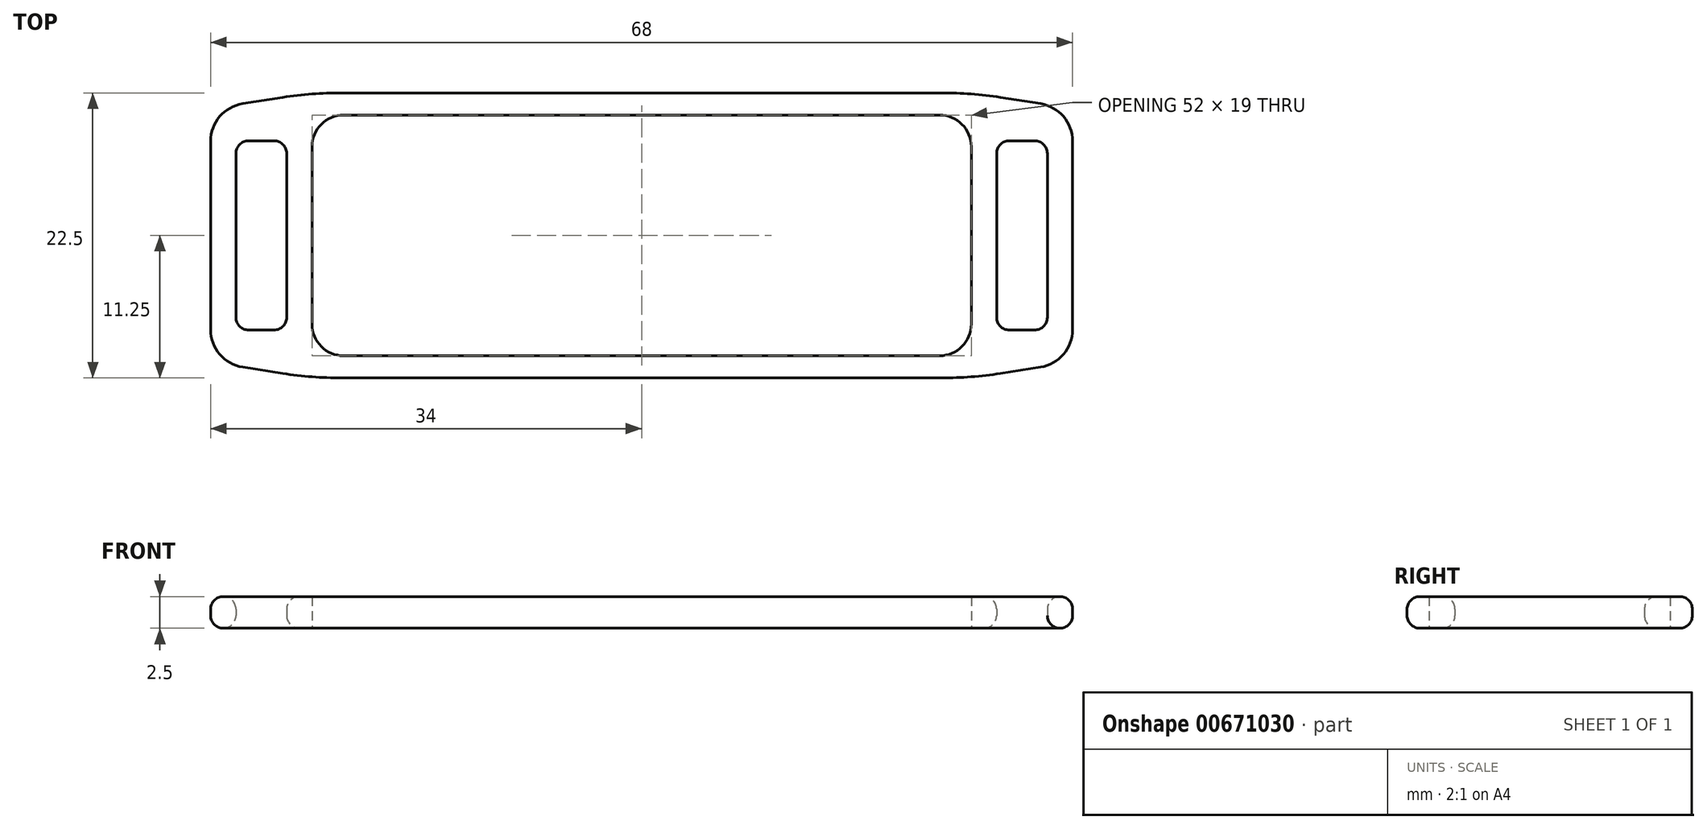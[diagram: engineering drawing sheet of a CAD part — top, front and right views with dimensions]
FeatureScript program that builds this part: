
annotation { "Feature Type Name" : "Feature", "Feature Type Description" : "" }
export const myFeature = defineFeature(function(context is Context, id is Id, definition is map)
    precondition{}
    {
        {
            var Q0;
            Q0=qCreatedBy(makeId("Top.planeOp"),FACE);
            var sketch = newSketch(context, id + "F0", { "sketchPlane" : qUnion([Q0])});
            skLineSegment(sketch, "E0.bottom", {"start": v(23.5, 9.5) * mm, "end": v(-23.5, 9.5) * mm});
            skLineSegment(sketch, "E0.top", {"start": v(23.5, -9.5) * mm, "end": v(-23.5, -9.5) * mm});
            skLineSegment(sketch, "E0.left", {"start": v(26, 7) * mm, "end": v(26, -7) * mm});
            skLineSegment(sketch, "E0.right", {"start": v(-26, 7) * mm, "end": v(-26, -7) * mm});
            skPoint(sketch, "E0.middle", {"position": v(0, 0) * mm});
            skPoint(sketch, "E1.visualSharp", {"position": v(-26, 9.5) * mm});
            skArc(sketch, "E1.filletArc", {"start": v(-23.5, 9.5) * mm, "mid": v(-25.27, 8.77) * mm, "end": v(-26, 7) * mm});
            skPoint(sketch, "E2.visualSharp", {"position": v(26, 9.5) * mm});
            skArc(sketch, "E2.filletArc", {"start": v(26, 7) * mm, "mid": v(25.27, 8.77) * mm, "end": v(23.5, 9.5) * mm});
            skPoint(sketch, "E3.visualSharp", {"position": v(26, -9.5) * mm});
            skArc(sketch, "E3.filletArc", {"start": v(23.5, -9.5) * mm, "mid": v(25.27, -8.77) * mm, "end": v(26, -7) * mm});
            skPoint(sketch, "E4.visualSharp", {"position": v(-26, -9.5) * mm});
            skArc(sketch, "E4.filletArc", {"start": v(-26, -7) * mm, "mid": v(-25.27, -8.77) * mm, "end": v(-23.5, -9.5) * mm});
            skLineSegment(sketch, "E5.bottom", {"start": v(34, -11.25) * mm, "end": v(-34, -11.25) * mm});
            skLineSegment(sketch, "E5.top", {"start": v(34, 11.25) * mm, "end": v(-34, 11.25) * mm});
            skLineSegment(sketch, "E5.left", {"start": v(34, -11.25) * mm, "end": v(34, 11.25) * mm});
            skLineSegment(sketch, "E5.right", {"start": v(-34, -11.25) * mm, "end": v(-34, 11.25) * mm});
            skLineSegment(sketch, "E6", {"start": v(26, 11.25) * mm, "end": v(34, 10) * mm});
            skLineSegment(sketch, "E7.MirrorCS", {"start": v(26, -11.25) * mm, "end": v(34, -10) * mm});
            skLineSegment(sketch, "E8.MirrorCS", {"start": v(-26, 11.25) * mm, "end": v(-34, 10) * mm});
            skLineSegment(sketch, "E9.MirrorCS", {"start": v(-26, -11.25) * mm, "end": v(-34, -10) * mm});
            skLineSegment(sketch, "E10.bottom", {"start": v(31, -7.47) * mm, "end": v(29, -7.47) * mm});
            skLineSegment(sketch, "E10.top", {"start": v(31, 7.47) * mm, "end": v(29, 7.47) * mm});
            skLineSegment(sketch, "E10.left", {"start": v(32, -6.47) * mm, "end": v(32, 6.47) * mm});
            skLineSegment(sketch, "E10.right", {"start": v(28, -6.47) * mm, "end": v(28, 6.47) * mm});
            skPoint(sketch, "E10.middle", {"position": v(30, 0) * mm});
            skPoint(sketch, "E11.visualSharp", {"position": v(32, 7.47) * mm});
            skArc(sketch, "E11.filletArc", {"start": v(32, 6.47) * mm, "mid": v(31.7, 7.18) * mm, "end": v(31, 7.47) * mm});
            skPoint(sketch, "E12.visualSharp", {"position": v(32, -7.47) * mm});
            skArc(sketch, "E12.filletArc", {"start": v(31, -7.47) * mm, "mid": v(31.7, -7.18) * mm, "end": v(32, -6.47) * mm});
            skPoint(sketch, "E13.visualSharp", {"position": v(28, -7.47) * mm});
            skArc(sketch, "E13.filletArc", {"start": v(28, -6.47) * mm, "mid": v(28.3, -7.18) * mm, "end": v(29, -7.47) * mm});
            skPoint(sketch, "E14.visualSharp", {"position": v(28, 7.47) * mm});
            skArc(sketch, "E14.filletArc", {"start": v(29, 7.47) * mm, "mid": v(28.3, 7.18) * mm, "end": v(28, 6.47) * mm});
            skLineSegment(sketch, "E15", {"start": v(31, -6.47) * mm, "end": v(31, -12.4) * mm, "construction": true});
            skPoint(sketch, "E16", {"position": v(31, -10.47) * mm});
            skArc(sketch, "E17.MirrorCS", {"start": v(-32, 6.47) * mm, "mid": v(-31.7, 7.18) * mm, "end": v(-31, 7.47) * mm});
            skArc(sketch, "E18.MirrorCS", {"start": v(-28, -6.47) * mm, "mid": v(-28.3, -7.18) * mm, "end": v(-29, -7.47) * mm});
            skArc(sketch, "E19.MirrorCS", {"start": v(-31, -7.47) * mm, "mid": v(-31.7, -7.18) * mm, "end": v(-32, -6.47) * mm});
            skArc(sketch, "E20.MirrorCS", {"start": v(-29, 7.47) * mm, "mid": v(-28.3, 7.18) * mm, "end": v(-28, 6.47) * mm});
            skPoint(sketch, "E21.MirrorP", {"position": v(-32, 7.47) * mm});
            skPoint(sketch, "E22.MirrorP", {"position": v(-32, -7.47) * mm});
            skLineSegment(sketch, "E23.MirrorCS", {"start": v(-32, -6.47) * mm, "end": v(-32, 6.47) * mm});
            skLineSegment(sketch, "E24.MirrorCS", {"start": v(-31, -7.47) * mm, "end": v(-29, -7.47) * mm});
            skLineSegment(sketch, "E25.MirrorCS", {"start": v(-31, 7.47) * mm, "end": v(-29, 7.47) * mm});
            skPoint(sketch, "E26.MirrorP", {"position": v(-28, 7.47) * mm});
            skPoint(sketch, "E27.MirrorP", {"position": v(-30, 0) * mm});
            skPoint(sketch, "E28.MirrorP", {"position": v(-28, -7.47) * mm});
            skLineSegment(sketch, "E29.MirrorCS", {"start": v(-28, -6.47) * mm, "end": v(-28, 6.47) * mm});
            skSolve(sketch);
        }
        {
            var Q0;
            Q0=makeQuery(id+"F0.imprint","IMPRINT",FACE,{"disambiguationData":[TD([[makeQuery(id+"F0.imprint","IMPRINT",EDGE,{"derivedFrom":sQuery(id+"F0.wireOp",EDGE,"E0.bottom")}),-1.0]])]});
            extrude(context, id + "F1", {"entities" : qUnion([Q0]), "depth" : 2.5 * mm, "offsetDistance" : 25 * mm});
        }
        {
            var Q0;
            Q0=makeQuery(id+"F1.opExtrude","SWEPT_EDGE",EDGE,{"disambiguationData":[OSD([sQuery(id+"F0.wireOp",EDGE,"E5.left"),sQuery(id+"F0.wireOp",EDGE,"E7.MirrorCS")])]});
            var Q1;
            Q1=makeQuery(id+"F1.opExtrude","SWEPT_EDGE",EDGE,{"disambiguationData":[OSD([sQuery(id+"F0.wireOp",EDGE,"E5.left"),sQuery(id+"F0.wireOp",EDGE,"E6")])]});
            var Q2;
            Q2=makeQuery(id+"F1.opExtrude","SWEPT_EDGE",EDGE,{"disambiguationData":[OSD([sQuery(id+"F0.wireOp",EDGE,"E5.right"),sQuery(id+"F0.wireOp",EDGE,"E9.MirrorCS")])]});
            var Q3;
            Q3=makeQuery(id+"F1.opExtrude","SWEPT_EDGE",EDGE,{"disambiguationData":[OSD([sQuery(id+"F0.wireOp",EDGE,"E5.right"),sQuery(id+"F0.wireOp",EDGE,"E8.MirrorCS")])]});
            fillet(context, id + "F2", {"entities" : qUnion([Q0, Q1, Q2, Q3]), "radius" : 3 * mm, "allowEdgeOverflow" : false});
        }
        {
            var Q0;
            Q0=makeQuery(id+"F1.opExtrude","SWEPT_EDGE",EDGE,{"disambiguationData":[OSD([sQuery(id+"F0.wireOp",EDGE,"E5.bottom"),sQuery(id+"F0.wireOp",EDGE,"E9.MirrorCS")])]});
            var Q1;
            Q1=makeQuery(id+"F1.opExtrude","SWEPT_EDGE",EDGE,{"disambiguationData":[OSD([sQuery(id+"F0.wireOp",EDGE,"E5.bottom"),sQuery(id+"F0.wireOp",EDGE,"E7.MirrorCS")])]});
            var Q2;
            Q2=makeQuery(id+"F1.opExtrude","SWEPT_EDGE",EDGE,{"disambiguationData":[OSD([sQuery(id+"F0.wireOp",EDGE,"E5.top"),sQuery(id+"F0.wireOp",EDGE,"E8.MirrorCS")])]});
            var Q3;
            Q3=makeQuery(id+"F1.opExtrude","SWEPT_EDGE",EDGE,{"disambiguationData":[OSD([sQuery(id+"F0.wireOp",EDGE,"E5.top"),sQuery(id+"F0.wireOp",EDGE,"E6")])]});
            fillet(context, id + "F3", {"entities" : qUnion([Q0, Q1, Q2, Q3]), "radius" : 30 * mm, "allowEdgeOverflow" : false});
        }
        {
            var Q0;
            Q0=makeQuery(id+"F1.opExtrude","CAP_EDGE",EDGE,{"disambiguationData":[OSD([sQuery(id+"F0.wireOp",EDGE,"E5.bottom")])],"isStart":false});
            var Q1;
            Q1=makeQuery(id+"F1.opExtrude","CAP_EDGE",EDGE,{"disambiguationData":[OSD([sQuery(id+"F0.wireOp",EDGE,"E10.right")])],"isStart":false});
            var Q2;
            Q2=makeQuery(id+"F1.opExtrude","CAP_EDGE",EDGE,{"disambiguationData":[OSD([sQuery(id+"F0.wireOp",EDGE,"E23.MirrorCS")])],"isStart":false});
            var Q3;
            Q3=makeQuery(id+"F1.opExtrude","CAP_EDGE",EDGE,{"disambiguationData":[OSD([sQuery(id+"F0.wireOp",EDGE,"E25.MirrorCS")])],"isStart":true});
            var Q4;
            Q4=makeQuery(id+"F1.opExtrude","CAP_EDGE",EDGE,{"disambiguationData":[OSD([sQuery(id+"F0.wireOp",EDGE,"E10.top")])],"isStart":true});
            var Q5;
            {var subQ0=sQuery(id+"F0.wireOp",EDGE,"E7.MirrorCS");var subQ1=sQuery(id+"F0.wireOp",EDGE,"E5.left");Q5=makeQuery(id+"F2.opFillet","BLEND_EDGE",EDGE,{"blendedFrom":[makeQuery(id+"F1.opExtrude","SWEPT_EDGE",EDGE,{"disambiguationData":[OSD([subQ1,subQ0])]}),makeQuery(id+"F1.opExtrude","CAP_FACE",FACE,{"disambiguationData":[OSD([sQuery(id+"F0.wireOp",EDGE,"E0.bottom"),sQuery(id+"F0.wireOp",EDGE,"E0.top"),sQuery(id+"F0.wireOp",EDGE,"E0.left"),sQuery(id+"F0.wireOp",EDGE,"E0.right"),sQuery(id+"F0.wireOp",EDGE,"E1.filletArc"),sQuery(id+"F0.wireOp",EDGE,"E2.filletArc"),sQuery(id+"F0.wireOp",EDGE,"E3.filletArc"),sQuery(id+"F0.wireOp",EDGE,"E4.filletArc"),sQuery(id+"F0.wireOp",EDGE,"E5.bottom"),sQuery(id+"F0.wireOp",EDGE,"E5.top"),subQ1,sQuery(id+"F0.wireOp",EDGE,"E5.right"),sQuery(id+"F0.wireOp",EDGE,"E6"),subQ0,sQuery(id+"F0.wireOp",EDGE,"E8.MirrorCS"),sQuery(id+"F0.wireOp",EDGE,"E9.MirrorCS"),sQuery(id+"F0.wireOp",EDGE,"E10.bottom"),sQuery(id+"F0.wireOp",EDGE,"E10.top"),sQuery(id+"F0.wireOp",EDGE,"E10.left"),sQuery(id+"F0.wireOp",EDGE,"E10.right"),sQuery(id+"F0.wireOp",EDGE,"E11.filletArc"),sQuery(id+"F0.wireOp",EDGE,"E12.filletArc"),sQuery(id+"F0.wireOp",EDGE,"E13.filletArc"),sQuery(id+"F0.wireOp",EDGE,"E14.filletArc"),sQuery(id+"F0.wireOp",EDGE,"E17.MirrorCS"),sQuery(id+"F0.wireOp",EDGE,"E18.MirrorCS"),sQuery(id+"F0.wireOp",EDGE,"E19.MirrorCS"),sQuery(id+"F0.wireOp",EDGE,"E20.MirrorCS"),sQuery(id+"F0.wireOp",EDGE,"E23.MirrorCS"),sQuery(id+"F0.wireOp",EDGE,"E24.MirrorCS"),sQuery(id+"F0.wireOp",EDGE,"E25.MirrorCS"),sQuery(id+"F0.wireOp",EDGE,"E29.MirrorCS")])],"isStart":true})],"blendedInto":[makeQuery(id+"F1.opExtrude","CAP_FACE",FACE,{"disambiguationData":[OSD([sQuery(id+"F0.wireOp",EDGE,"E0.bottom"),sQuery(id+"F0.wireOp",EDGE,"E0.top"),sQuery(id+"F0.wireOp",EDGE,"E0.left"),sQuery(id+"F0.wireOp",EDGE,"E0.right"),sQuery(id+"F0.wireOp",EDGE,"E1.filletArc"),sQuery(id+"F0.wireOp",EDGE,"E2.filletArc"),sQuery(id+"F0.wireOp",EDGE,"E3.filletArc"),sQuery(id+"F0.wireOp",EDGE,"E4.filletArc"),sQuery(id+"F0.wireOp",EDGE,"E5.bottom"),sQuery(id+"F0.wireOp",EDGE,"E5.top"),subQ1,sQuery(id+"F0.wireOp",EDGE,"E5.right"),sQuery(id+"F0.wireOp",EDGE,"E6"),subQ0,sQuery(id+"F0.wireOp",EDGE,"E8.MirrorCS"),sQuery(id+"F0.wireOp",EDGE,"E9.MirrorCS"),sQuery(id+"F0.wireOp",EDGE,"E10.bottom"),sQuery(id+"F0.wireOp",EDGE,"E10.top"),sQuery(id+"F0.wireOp",EDGE,"E10.left"),sQuery(id+"F0.wireOp",EDGE,"E10.right"),sQuery(id+"F0.wireOp",EDGE,"E11.filletArc"),sQuery(id+"F0.wireOp",EDGE,"E12.filletArc"),sQuery(id+"F0.wireOp",EDGE,"E13.filletArc"),sQuery(id+"F0.wireOp",EDGE,"E14.filletArc"),sQuery(id+"F0.wireOp",EDGE,"E17.MirrorCS"),sQuery(id+"F0.wireOp",EDGE,"E18.MirrorCS"),sQuery(id+"F0.wireOp",EDGE,"E19.MirrorCS"),sQuery(id+"F0.wireOp",EDGE,"E20.MirrorCS"),sQuery(id+"F0.wireOp",EDGE,"E23.MirrorCS"),sQuery(id+"F0.wireOp",EDGE,"E24.MirrorCS"),sQuery(id+"F0.wireOp",EDGE,"E25.MirrorCS"),sQuery(id+"F0.wireOp",EDGE,"E29.MirrorCS")])],"isStart":true})]});}
            fillet(context, id + "F4", {"entities" : qUnion([Q0, Q1, Q2, Q3, Q4, Q5]), "radius" : 1 * mm, "tangentPropagation" : true, "allowEdgeOverflow" : false});
        }
    });
